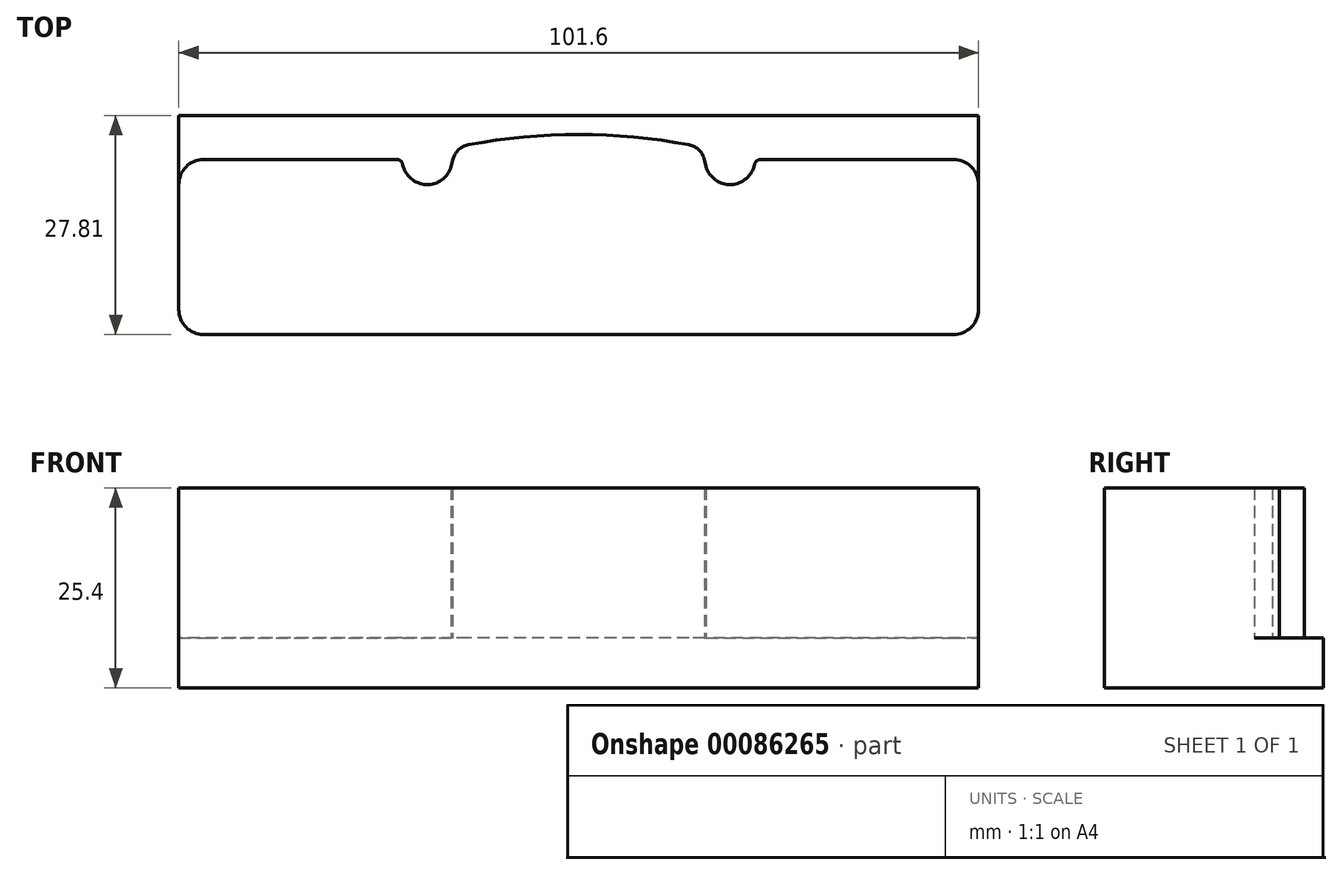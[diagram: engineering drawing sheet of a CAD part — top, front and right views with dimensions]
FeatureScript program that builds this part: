
annotation { "Feature Type Name" : "Feature", "Feature Type Description" : "" }
export const myFeature = defineFeature(function(context is Context, id is Id, definition is map)
    precondition{}
    {
        {
            var Q0;
            Q0=qCreatedBy(makeId("Top.planeOp"),FACE);
            var sketch = newSketch(context, id + "F0", { "sketchPlane" : qUnion([Q0])});
            skLineSegment(sketch, "E0.bottom", {"start": v(50.8, -12.7) * mm, "end": v(-50.8, -12.7) * mm});
            skLineSegment(sketch, "E0.left", {"start": v(50.8, -12.7) * mm, "end": v(50.8, 9.53) * mm});
            skLineSegment(sketch, "E0.right", {"start": v(-50.8, -12.7) * mm, "end": v(-50.8, 9.52) * mm});
            skPoint(sketch, "E0.middle", {"position": v(0, 0) * mm});
            skLineSegment(sketch, "E1", {"start": v(-50.8, 9.52) * mm, "end": v(-23.09, 9.52) * mm});
            skLineSegment(sketch, "E2.trimOffspring", {"start": v(23.09, 9.53) * mm, "end": v(50.8, 9.53) * mm});
            skPoint(sketch, "E3.orphan", {"position": v(50.8, 12.7) * mm});
            skPoint(sketch, "E4.orphan", {"position": v(-50.8, 12.7) * mm});
            skArc(sketch, "E5.trimOffspring", {"start": v(13.98, 11.4) * mm, "mid": v(0, 12.7) * mm, "end": v(-13.98, 11.4) * mm});
            skArc(sketch, "E6", {"start": v(-22.34, 8.91) * mm, "mid": v(-19.37, 6.35) * mm, "end": v(-16.18, 8.62) * mm});
            skPoint(sketch, "E7.orphan", {"position": v(21.77, 9.53) * mm});
            skPoint(sketch, "E8.visualSharp", {"position": v(-16.05, 10.99) * mm});
            skArc(sketch, "E8.filletArc", {"start": v(-13.98, 11.4) * mm, "mid": v(-15.3, 10.7) * mm, "end": v(-16, 9.38) * mm});
            skPoint(sketch, "E9.visualSharp", {"position": v(16.05, 11) * mm});
            skArc(sketch, "E9.filletArc", {"start": v(16, 9.43) * mm, "mid": v(15.29, 10.73) * mm, "end": v(13.98, 11.4) * mm});
            skLineSegment(sketch, "E10", {"start": v(16, 9.43) * mm, "end": v(16.18, 8.62) * mm});
            skArc(sketch, "E11.trimOffspring", {"start": v(16.18, 8.62) * mm, "mid": v(19.37, 6.35) * mm, "end": v(22.34, 8.91) * mm});
            skPoint(sketch, "E12.start.orphan", {"position": v(16.05, 9.53) * mm});
            skLineSegment(sketch, "E13", {"start": v(0, 0) * mm, "end": v(0, 7.45) * mm});
            skLineSegment(sketch, "E14.MirrorCS", {"start": v(-16, 9.38) * mm, "end": v(-16.18, 8.62) * mm});
            skPoint(sketch, "E15.orphan", {"position": v(-16, 9.43) * mm});
            skPoint(sketch, "E16.visualSharp", {"position": v(-22.4, 9.52) * mm});
            skArc(sketch, "E16.filletArc", {"start": v(-22.34, 8.91) * mm, "mid": v(-22.6, 9.35) * mm, "end": v(-23.09, 9.52) * mm});
            skPoint(sketch, "E17.visualSharp", {"position": v(22.4, 9.53) * mm});
            skArc(sketch, "E17.filletArc", {"start": v(23.09, 9.53) * mm, "mid": v(22.6, 9.35) * mm, "end": v(22.34, 8.91) * mm});
            skSolve(sketch);
        }
        {
            var Q0;
            Q0 = qSketchRegion(id + "F0", true);
            extrude(context, id + "F1", {"entities" : qUnion([Q0]), "depth" : 19.05 * mm});
        }
        {
            var Q0;
            Q0=makeQuery(id+"F1.opExtrude","CAP_FACE",FACE,{"disambiguationData":[OSD([sQuery(id+"F0.wireOp",EDGE,"E0.bottom"),sQuery(id+"F0.wireOp",EDGE,"E0.left"),sQuery(id+"F0.wireOp",EDGE,"E0.right"),sQuery(id+"F0.wireOp",EDGE,"E1"),sQuery(id+"F0.wireOp",EDGE,"E2.trimOffspring"),sQuery(id+"F0.wireOp",EDGE,"E5.trimOffspring")])],"isStart":true});
            var sketch = newSketch(context, id + "F2", { "sketchPlane" : qUnion([Q0])});
            skLineSegment(sketch, "E18.top", {"start": v(50.8, -15.11) * mm, "end": v(-50.8, -15.11) * mm});
            skLineSegment(sketch, "E18.left", {"start": v(50.8, 12.7) * mm, "end": v(50.8, -15.11) * mm});
            skLineSegment(sketch, "E18.right", {"start": v(-50.8, 12.7) * mm, "end": v(-50.8, -15.11) * mm});
            skPoint(sketch, "E18.middle", {"position": v(0, 0) * mm});
            skLineSegment(sketch, "E19", {"start": v(50.8, 12.7) * mm, "end": v(-50.8, 12.7) * mm});
            skPoint(sketch, "E18.bottom.start.orphan", {"position": v(50.8, 15.11) * mm});
            skPoint(sketch, "E20.orphan", {"position": v(-50.8, 15.11) * mm});
            skSolve(sketch);
        }
        {
            var Q0;
            Q0 = qSketchRegion(id + "F2", true);
            extrude(context, id + "F3", {"entities" : qUnion([Q0]), "operationType" : NewBodyOperationType.ADD, "depth" : 6.35 * mm});
        }
        {
            var Q0;
            Q0=makeQuery(id+"F1.opExtrude","SWEPT_EDGE",EDGE,{"disambiguationData":[OSD([sQuery(id+"F0.wireOp",EDGE,"E0.left"),sQuery(id+"F0.wireOp",EDGE,"E2.trimOffspring")])]});
            var Q1;
            Q1=makeQuery(id+"F1.opExtrude","SWEPT_EDGE",EDGE,{"disambiguationData":[OSD([sQuery(id+"F0.wireOp",EDGE,"E0.right"),sQuery(id+"F0.wireOp",EDGE,"E1")])]});
            var Q2;
            Q2=makeQuery(id+"F3.boolean.opBoolean","MERGE",EDGE,{"derivedFrom":[makeQuery(id+"F1.opExtrude","SWEPT_EDGE",EDGE,{"disambiguationData":[OSD([sQuery(id+"F0.wireOp",EDGE,"E0.bottom"),sQuery(id+"F0.wireOp",EDGE,"E0.right")])]}),makeQuery(id+"F3.opExtrude","SWEPT_EDGE",EDGE,{"disambiguationData":[OSD([sQuery(id+"F2.wireOp",EDGE,"E18.right"),sQuery(id+"F2.wireOp",EDGE,"E19")])]})]});
            var Q3;
            Q3=makeQuery(id+"F3.boolean.opBoolean","MERGE",EDGE,{"derivedFrom":[makeQuery(id+"F1.opExtrude","SWEPT_EDGE",EDGE,{"disambiguationData":[OSD([sQuery(id+"F0.wireOp",EDGE,"E0.bottom"),sQuery(id+"F0.wireOp",EDGE,"E0.left")])]}),makeQuery(id+"F3.opExtrude","SWEPT_EDGE",EDGE,{"disambiguationData":[OSD([sQuery(id+"F2.wireOp",EDGE,"E18.left"),sQuery(id+"F2.wireOp",EDGE,"E19")])]})]});
            fillet(context, id + "F4", {"entities" : qUnion([Q0, Q1, Q2, Q3]), "radius" : 3.17 * mm, "tangentPropagation" : true, "allowEdgeOverflow" : false});
        }
    });
